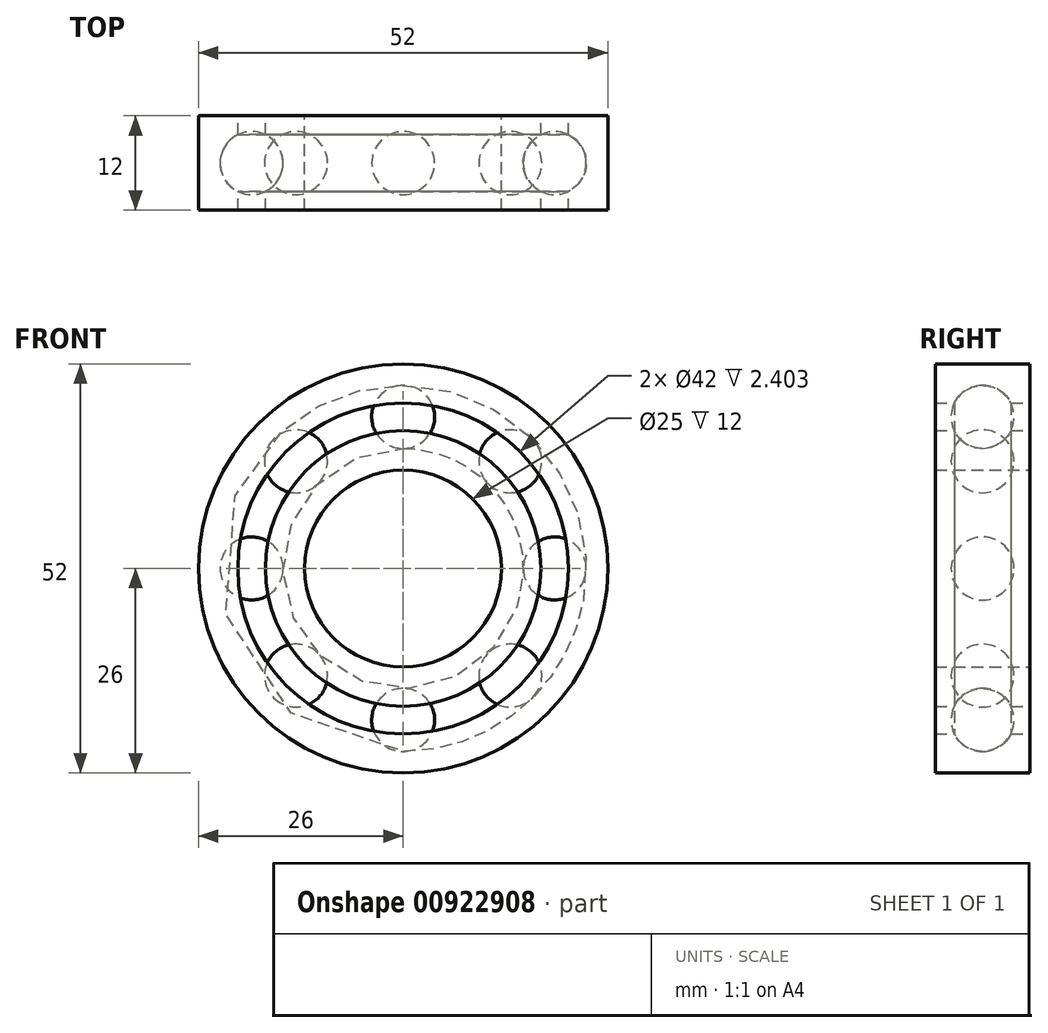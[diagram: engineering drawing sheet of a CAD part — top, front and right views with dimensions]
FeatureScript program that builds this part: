
annotation { "Feature Type Name" : "Feature", "Feature Type Description" : "" }
export const myFeature = defineFeature(function(context is Context, id is Id, definition is map)
    precondition{}
    {
        {
            var Q0;
            Q0=qCreatedBy(makeId("Right.planeOp"),FACE);
            var sketch = newSketch(context, id + "F0", { "sketchPlane" : qUnion([Q0])});
            skLineSegment(sketch, "E0", {"start": v(0, -26) * mm, "end": v(-6, -26) * mm});
            skLineSegment(sketch, "E1", {"start": v(-6, -26) * mm, "end": v(-6, -21) * mm});
            skLineSegment(sketch, "E2.MirrorCS", {"start": v(6, -26) * mm, "end": v(6, -21) * mm});
            skPoint(sketch, "E3.start.orphan", {"position": v(0, 0) * mm});
            skLineSegment(sketch, "E4", {"start": v(-6, -21) * mm, "end": v(-3.6, -21) * mm});
            skLineSegment(sketch, "E5", {"start": v(0, 0) * mm, "end": v(0, -12.5) * mm, "construction": true});
            skArc(sketch, "E6", {"start": v(3.6, -17.5) * mm, "mid": v(0, -15.25) * mm, "end": v(-3.6, -17.5) * mm});
            skLineSegment(sketch, "E7", {"start": v(-6, -17.5) * mm, "end": v(-6, -12.5) * mm});
            skLineSegment(sketch, "E8", {"start": v(-6, -12.5) * mm, "end": v(6, -12.5) * mm});
            skLineSegment(sketch, "E9", {"start": v(6, -17.5) * mm, "end": v(6, -12.5) * mm});
            skLineSegment(sketch, "E10", {"start": v(-6, -17.5) * mm, "end": v(-3.6, -17.5) * mm});
            skLineSegment(sketch, "E11", {"start": v(6, -26) * mm, "end": v(0, -26) * mm});
            skLineSegment(sketch, "E12.trimOffspring", {"start": v(3.6, -17.5) * mm, "end": v(6, -17.5) * mm});
            skLineSegment(sketch, "E13.trimOffspring", {"start": v(3.6, -21) * mm, "end": v(6, -21) * mm});
            skArc(sketch, "E14.trimOffspring", {"start": v(-3.6, -21) * mm, "mid": v(0, -23.25) * mm, "end": v(3.6, -21) * mm});
            skLineSegment(sketch, "E15", {"start": v(0, 0) * mm, "end": v(-18.25, 0) * mm, "construction": true});
            skSolve(sketch);
        }
        {
            var Q0;
            Q0=makeQuery(id+"F0.imprint","IMPRINT",FACE,{"disambiguationData":[TD([[makeQuery(id+"F0.imprint","IMPRINT",EDGE,{"derivedFrom":sQuery(id+"F0.wireOp",EDGE,"E6")}),-1.0]])]});
            var Q1;
            Q1=makeQuery(id+"F0.imprint","IMPRINT",FACE,{"disambiguationData":[TD([[makeQuery(id+"F0.imprint","IMPRINT",EDGE,{"derivedFrom":sQuery(id+"F0.wireOp",EDGE,"E0")}),-1.0]])]});
            var Q2;
            Q2=sQuery(id+"F0.wireOp",EDGE,"E15");
            var Q3;
            Q3=sQuery(id+"F0.wireOp",EDGE,"E15");
            revolve(context, id + "F1", {"surfaceOperationType" : NewSurfaceOperationType.NEW, "entities" : qUnion([Q0, Q1]), "surfaceEntities" : qUnion([Q2]), "axis" : qUnion([Q3]), "revolveType" : RevolveType.FULL});
        }
        {
            var Q0;
            Q0=qCreatedBy(makeId("Front.planeOp"),FACE);
            var sketch = newSketch(context, id + "F2", { "sketchPlane" : qUnion([Q0])});
            skArc(sketch, "E16", {"start": v(0, -15.25) * mm, "mid": v(-4, -19.25) * mm, "end": v(0, -23.25) * mm});
            skLineSegment(sketch, "E17", {"start": v(0, -19.25) * mm, "end": v(0, -6.22) * mm, "construction": true});
            skLineSegment(sketch, "E18", {"start": v(0, -23.25) * mm, "end": v(0, -15.25) * mm});
            skSolve(sketch);
        }
        {
            var Q0;
            Q0 = qSketchRegion(id + "F2", true);
            var Q1;
            Q1=sQuery(id+"F2.wireOp",EDGE,"E17");
            revolve(context, id + "F3", {"surfaceOperationType" : NewSurfaceOperationType.NEW, "entities" : qUnion([Q0]), "axis" : qUnion([Q1]), "revolveType" : RevolveType.FULL});
        }
        {
            var Q0;
            Q0=qCreatedBy(makeId("Right.planeOp"),FACE);
            var sketch = newSketch(context, id + "F4", { "sketchPlane" : qUnion([Q0])});
            skLineSegment(sketch, "E19", {"start": v(0, 0) * mm, "end": v(-20.16, 0) * mm, "construction": true});
            skSolve(sketch);
        }
        {
            var Q0;
            Q0=makeQuery(id+"F3.opRevolve","SWEPT_BODY",BODY,{"disambiguationData":[OSD([sQuery(id+"F2.wireOp",EDGE,"E16"),sQuery(id+"F2.wireOp",EDGE,"E18")])]});
            var Q1;
            Q1=sQuery(id+"F4.wireOp",EDGE,"E19");
            circularPattern(context, id + "F5", {"entities" : qUnion([Q0]), "axis" : qUnion([Q1]), "angle" : 360 * degree, "instanceCount" : 8, "equalSpace" : true});
        }
    });
